# Revit family: Sanitary_Basins_Roca_INSPIRA-ROUND-500-Over-countertop
name_source: partatom
category: Plumbing Fixtures
units: mm (PartAtom-declared; Revit-internal decimal feet)

## family parameters
Always vertical = No
Cut with Voids When Loaded = No
OmniClass Number = 23.45.00.00
OmniClass Title = Sanitary, Laundry, and Cleaning Equipment
Part Type = Normal
Room Calculation Point = No
Round Connector Dimension = Use Diameter
Shared = No
Work Plane-Based = No

## types (1)
- Sanitary_Basins_Roca_INSPIRA-ROUND-500-Over-countertop
    BIMobject category = Basins
    BIMobject category code = sanitary-basins
    BIMobject main category = Sanitary
    BIMobject main category code = sanitary
    BOSUseNativeGeometries = 1
    Brand url = http://www.roca.es
    Default Elevation = 0 mm  [stored 0 ft]
    Design country = Spain
    Edition number = 1
    IFC Classification = Furnishing Element
    Manufacturer name = Roca
    Material main = Vitreous china
    NBS Reference Code = 35-65-70-94
    NBS Reference Description = Wash Basin Systems
    Product Guid = 357640db-bab1-4ff3-84a4-b4e40d4e759c
    Product SKU = 327520xx0
    Product data url = https://bimobject.com
    Product family = INSPIRA
    Product group = Basins
    Product name = INSPIRA ROUND - 500 Over countertop FINECERAMIC® basin
    Product url = http://www.roca.com
    QR code = http://bimobject.com
    Technical description = http://www.roca.com
    UNSPSC Code = 301815
    Uniclass 1.4 Code = L7212
    Uniclass 1.4 Description = Washbasins
    Uniclass 2.0 Code = SS-35-65-70-94
    Uniclass 2.0 Description = Wash Basin Systems
    Youtube clip = https://www.youtube.com

note: [stored X ft] marks values corroborated as IEEE doubles in the binary element streams (Revit-internal decimal feet)

## geometry (parser evidence)
native form markers: Sweep x2
no freeform markers — native parametric forms only
